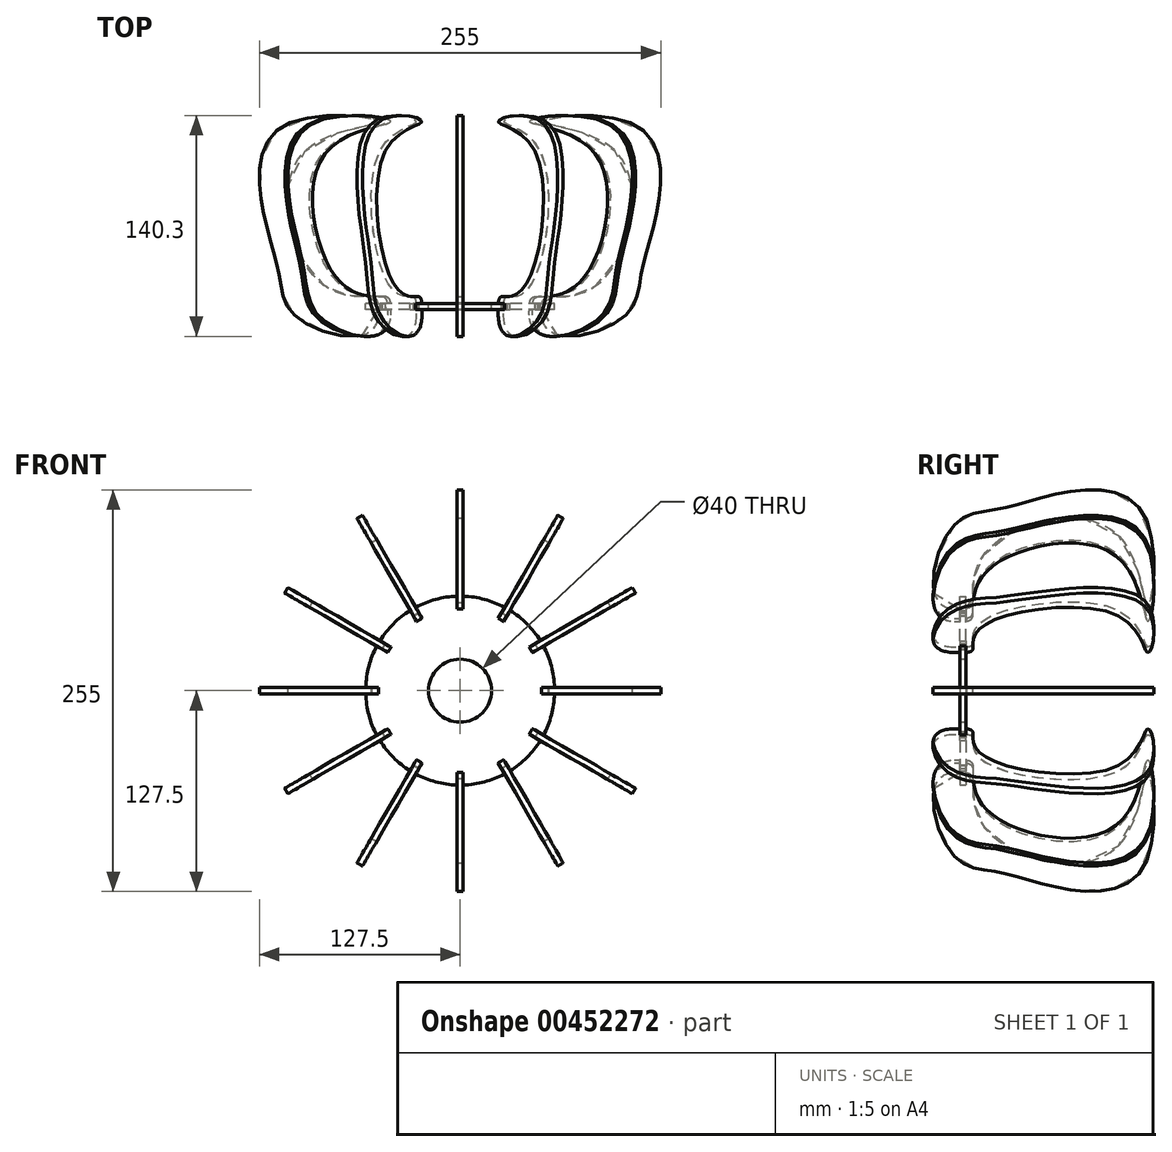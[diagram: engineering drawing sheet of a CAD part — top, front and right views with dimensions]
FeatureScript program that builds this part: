
annotation { "Feature Type Name" : "Feature", "Feature Type Description" : "" }
export const myFeature = defineFeature(function(context is Context, id is Id, definition is map)
    precondition{}
    {
        {
            var Q0;
            Q0=qCreatedBy(makeId("Front.planeOp"),FACE);
            var sketch = newSketch(context, id + "F0", { "sketchPlane" : qUnion([Q0])});
            skCircle(sketch, "E0", {"center": v(0, 0) * mm, "radius": 20 * mm});
            skArc(sketch, "E1", {"start": v(-2, 59.97) * mm, "mid": v(-15.53, 57.96) * mm, "end": v(-28.25, 52.93) * mm});
            skLineSegment(sketch, "E2", {"start": v(-2, 59.97) * mm, "end": v(-2, 55.97) * mm});
            skLineSegment(sketch, "E3", {"start": v(-2, 55.97) * mm, "end": v(2, 55.97) * mm});
            skLineSegment(sketch, "E4", {"start": v(2, 55.97) * mm, "end": v(2, 59.97) * mm});
            skLineSegment(sketch, "E5.1.0", {"start": v(-26.25, 49.47) * mm, "end": v(-28.25, 52.93) * mm});
            skLineSegment(sketch, "E5.1.1", {"start": v(-29.72, 47.47) * mm, "end": v(-26.25, 49.47) * mm});
            skLineSegment(sketch, "E5.1.2", {"start": v(-31.72, 50.93) * mm, "end": v(-29.72, 47.47) * mm});
            skLineSegment(sketch, "E5.2.0", {"start": v(-47.47, 29.72) * mm, "end": v(-50.93, 31.72) * mm});
            skLineSegment(sketch, "E5.2.1", {"start": v(-49.47, 26.25) * mm, "end": v(-47.47, 29.72) * mm});
            skLineSegment(sketch, "E5.2.2", {"start": v(-52.93, 28.25) * mm, "end": v(-49.47, 26.25) * mm});
            skLineSegment(sketch, "E5.3.0", {"start": v(-55.97, 2) * mm, "end": v(-59.97, 2) * mm});
            skLineSegment(sketch, "E5.3.1", {"start": v(-55.97, -2) * mm, "end": v(-55.97, 2) * mm});
            skLineSegment(sketch, "E5.3.2", {"start": v(-59.97, -2) * mm, "end": v(-55.97, -2) * mm});
            skLineSegment(sketch, "E5.4.0", {"start": v(-49.47, -26.25) * mm, "end": v(-52.93, -28.25) * mm});
            skLineSegment(sketch, "E5.4.1", {"start": v(-47.47, -29.72) * mm, "end": v(-49.47, -26.25) * mm});
            skLineSegment(sketch, "E5.4.2", {"start": v(-50.93, -31.72) * mm, "end": v(-47.47, -29.72) * mm});
            skLineSegment(sketch, "E5.5.0", {"start": v(-29.72, -47.47) * mm, "end": v(-31.72, -50.93) * mm});
            skLineSegment(sketch, "E5.5.1", {"start": v(-26.25, -49.47) * mm, "end": v(-29.72, -47.47) * mm});
            skLineSegment(sketch, "E5.5.2", {"start": v(-28.25, -52.93) * mm, "end": v(-26.25, -49.47) * mm});
            skLineSegment(sketch, "E5.6.0", {"start": v(-2, -55.97) * mm, "end": v(-2, -59.97) * mm});
            skLineSegment(sketch, "E5.6.1", {"start": v(2, -55.97) * mm, "end": v(-2, -55.97) * mm});
            skLineSegment(sketch, "E5.6.2", {"start": v(2, -59.97) * mm, "end": v(2, -55.97) * mm});
            skLineSegment(sketch, "E5.7.0", {"start": v(26.25, -49.47) * mm, "end": v(28.25, -52.93) * mm});
            skLineSegment(sketch, "E5.7.1", {"start": v(29.72, -47.47) * mm, "end": v(26.25, -49.47) * mm});
            skLineSegment(sketch, "E5.7.2", {"start": v(31.72, -50.93) * mm, "end": v(29.72, -47.47) * mm});
            skLineSegment(sketch, "E5.8.0", {"start": v(47.47, -29.72) * mm, "end": v(50.93, -31.72) * mm});
            skLineSegment(sketch, "E5.8.1", {"start": v(49.47, -26.25) * mm, "end": v(47.47, -29.72) * mm});
            skLineSegment(sketch, "E5.8.2", {"start": v(52.93, -28.25) * mm, "end": v(49.47, -26.25) * mm});
            skLineSegment(sketch, "E5.9.0", {"start": v(55.97, -2) * mm, "end": v(59.97, -2) * mm});
            skLineSegment(sketch, "E5.9.1", {"start": v(55.97, 2) * mm, "end": v(55.97, -2) * mm});
            skLineSegment(sketch, "E5.9.2", {"start": v(59.97, 2) * mm, "end": v(55.97, 2) * mm});
            skLineSegment(sketch, "E5.10.0", {"start": v(49.47, 26.25) * mm, "end": v(52.93, 28.25) * mm});
            skLineSegment(sketch, "E5.10.1", {"start": v(47.47, 29.72) * mm, "end": v(49.47, 26.25) * mm});
            skLineSegment(sketch, "E5.10.2", {"start": v(50.93, 31.72) * mm, "end": v(47.47, 29.72) * mm});
            skLineSegment(sketch, "E5.11.0", {"start": v(29.72, 47.47) * mm, "end": v(31.72, 50.93) * mm});
            skLineSegment(sketch, "E5.11.1", {"start": v(26.25, 49.47) * mm, "end": v(29.72, 47.47) * mm});
            skLineSegment(sketch, "E5.11.2", {"start": v(28.25, 52.93) * mm, "end": v(26.25, 49.47) * mm});
            skArc(sketch, "E6.trimOffspring", {"start": v(-31.72, 50.93) * mm, "mid": v(-42.43, 42.43) * mm, "end": v(-50.93, 31.72) * mm});
            skArc(sketch, "E7.trimOffspring", {"start": v(-52.93, 28.25) * mm, "mid": v(-57.96, 15.53) * mm, "end": v(-59.97, 2) * mm});
            skArc(sketch, "E8.trimOffspring", {"start": v(28.25, 52.93) * mm, "mid": v(15.53, 57.96) * mm, "end": v(2, 59.97) * mm});
            skArc(sketch, "E9.trimOffspring", {"start": v(50.93, 31.72) * mm, "mid": v(42.43, 42.43) * mm, "end": v(31.72, 50.93) * mm});
            skArc(sketch, "E10.trimOffspring", {"start": v(-59.97, -2) * mm, "mid": v(-57.96, -15.53) * mm, "end": v(-52.93, -28.25) * mm});
            skArc(sketch, "E11.trimOffspring", {"start": v(-50.93, -31.72) * mm, "mid": v(-42.43, -42.43) * mm, "end": v(-31.72, -50.93) * mm});
            skArc(sketch, "E12.trimOffspring", {"start": v(59.97, 2) * mm, "mid": v(57.96, 15.53) * mm, "end": v(52.93, 28.25) * mm});
            skArc(sketch, "E13.trimOffspring", {"start": v(52.93, -28.25) * mm, "mid": v(57.96, -15.53) * mm, "end": v(59.97, -2) * mm});
            skArc(sketch, "E14.trimOffspring", {"start": v(31.72, -50.93) * mm, "mid": v(42.43, -42.43) * mm, "end": v(50.93, -31.72) * mm});
            skArc(sketch, "E15.trimOffspring", {"start": v(2, -59.97) * mm, "mid": v(15.53, -57.96) * mm, "end": v(28.25, -52.93) * mm});
            skArc(sketch, "E16.trimOffspring", {"start": v(-28.25, -52.93) * mm, "mid": v(-15.53, -57.96) * mm, "end": v(-2, -59.97) * mm});
            skSolve(sketch);
        }
        {
            var Q0;
            Q0=qSketchRegion(id+"F0",true);
            extrude(context, id + "F1", {"entities" : qUnion([Q0]), "endBound" : BoundingType.SYMMETRIC, "depth" : 4 * mm});
        }
        {
            var Q0;
            Q0=qCreatedBy(makeId("Top.planeOp"),FACE);
            var sketch = newSketch(context, id + "F2", { "sketchPlane" : qUnion([Q0])});
            skLineSegment(sketch, "E17.MirrorCS", {"start": v(52.09, 2.12) * mm, "end": v(56.09, 2) * mm});
            skLineSegment(sketch, "E18.MirrorCS", {"start": v(55.97, -2) * mm, "end": v(51.97, -1.88) * mm});
            skLineSegment(sketch, "E19.MirrorCS", {"start": v(56.09, 2) * mm, "end": v(55.97, -2) * mm});
            skFitSpline(sketch, "E20", {"points": [v(52.09, 2.12) * mm, v(62.75, 6.3) * mm, v(94.23, 20.99) * mm, v(99, 98.32) * mm, v(52.09, 117.57) * mm, v(111.17, 115.26) * mm, v(125.94, 65.3) * mm, v(115.08, 20.99) * mm, v(100.3, -9.42) * mm, v(51.97, -1.88) * mm], "startDerivative": vector(34.54, 272.37) * mm, "endDerivative": vector(63.67, 647.6) * mm});
            skSolve(sketch);
        }
        {
            var Q0;
            Q0=qSketchRegion(id+"F2",true);
            extrude(context, id + "F3", {"entities" : qUnion([Q0]), "endBound" : BoundingType.SYMMETRIC, "depth" : 4 * mm});
        }
        {
            var Q0;
            Q0=makeQuery(id+"F3.opExtrude","SWEPT_BODY",BODY,{"disambiguationData":[OSD([sQuery(id+"F2.wireOp",EDGE,"E17.MirrorCS"),sQuery(id+"F2.wireOp",EDGE,"E18.MirrorCS"),sQuery(id+"F2.wireOp",EDGE,"E19.MirrorCS"),sQuery(id+"F2.wireOp",EDGE,"E20")])]});
            var Q1;
            Q1=makeQuery(id+"F1.opExtrude","CAP_EDGE",EDGE,{"disambiguationData":[OSD([sQuery(id+"F0.wireOp",EDGE,"E0")])],"isStart":true});
            circularPattern(context, id + "F4", {"entities" : qUnion([Q0]), "axis" : qUnion([Q1]), "angle" : 360 * degree, "instanceCount" : 12, "equalSpace" : true});
        }
    });
